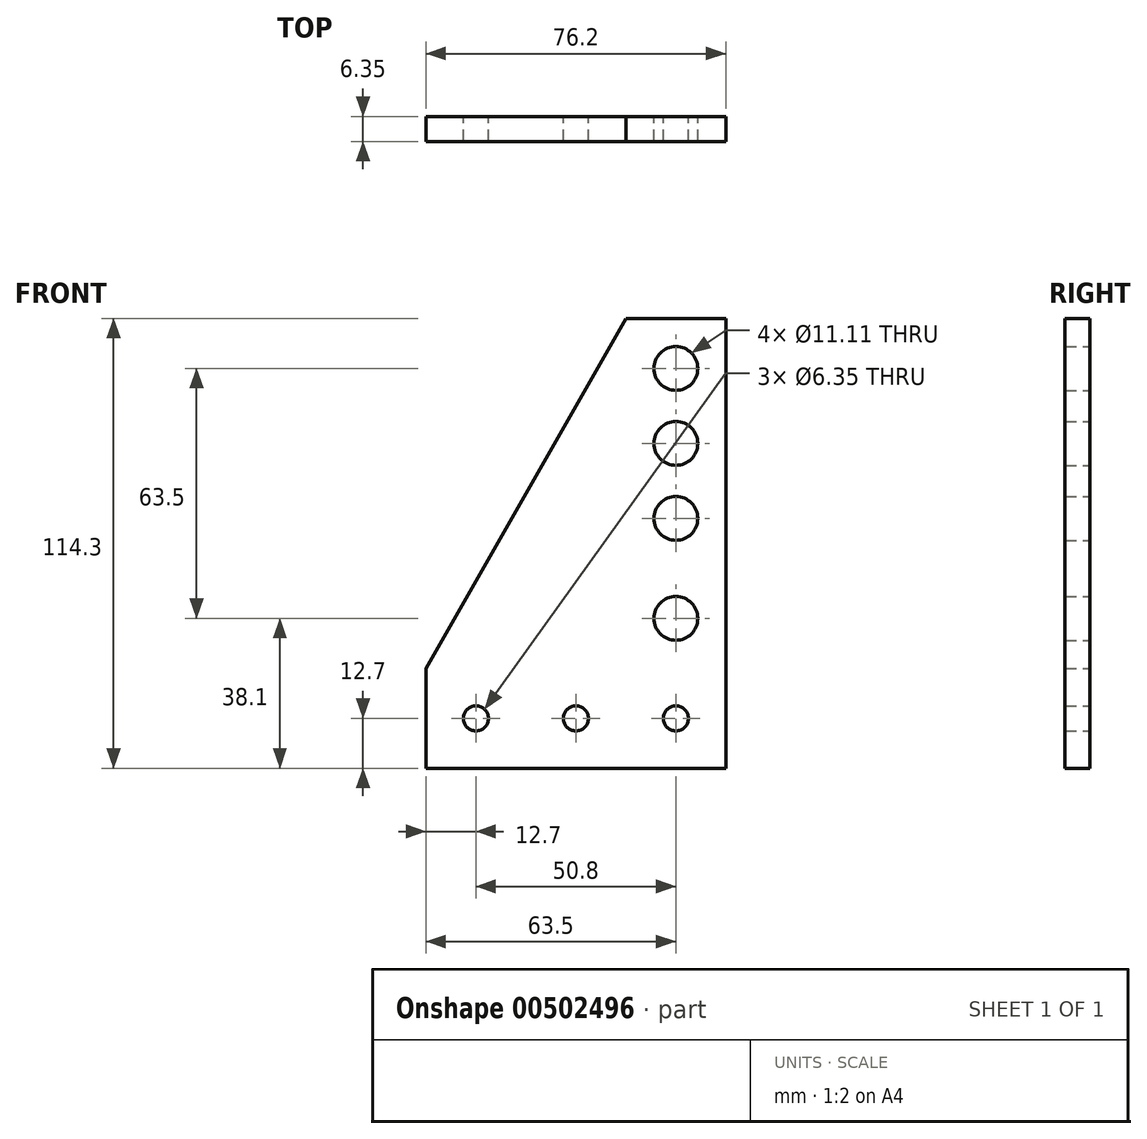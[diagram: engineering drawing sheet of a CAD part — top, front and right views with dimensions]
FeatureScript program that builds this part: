
annotation { "Feature Type Name" : "Feature", "Feature Type Description" : "" }
export const myFeature = defineFeature(function(context is Context, id is Id, definition is map)
    precondition{}
    {
        {
            var Q0;
            Q0=qCreatedBy(makeId("Front.planeOp"),FACE);
            var sketch = newSketch(context, id + "F0", { "sketchPlane" : qUnion([Q0])});
            skLineSegment(sketch, "E0.bottom", {"start": v(38.1, 57.15) * mm, "end": v(-38.1, 57.15) * mm});
            skLineSegment(sketch, "E0.top", {"start": v(38.1, -57.15) * mm, "end": v(-38.1, -57.15) * mm});
            skLineSegment(sketch, "E0.left", {"start": v(38.1, 57.15) * mm, "end": v(38.1, -57.15) * mm});
            skLineSegment(sketch, "E0.right", {"start": v(-38.1, 57.15) * mm, "end": v(-38.1, -57.15) * mm});
            skPoint(sketch, "E0.middle", {"position": v(0, 0) * mm});
            skLineSegment(sketch, "E1", {"start": v(-38.1, -44.45) * mm, "end": v(38.1, -44.45) * mm, "construction": true});
            skLineSegment(sketch, "E2", {"start": v(-38.1, -31.75) * mm, "end": v(38.1, -31.75) * mm, "construction": true});
            skCircle(sketch, "E3", {"center": v(-25.4, -44.45) * mm, "radius": 3.18 * mm});
            skCircle(sketch, "E4", {"center": v(0, -44.45) * mm, "radius": 3.18 * mm});
            skCircle(sketch, "E5", {"center": v(25.4, -44.45) * mm, "radius": 3.18 * mm});
            skLineSegment(sketch, "E6", {"start": v(25.4, -57.15) * mm, "end": v(25.4, 57.15) * mm, "construction": true});
            skCircle(sketch, "E7", {"center": v(25.4, -19.05) * mm, "radius": 5.56 * mm});
            skCircle(sketch, "E8", {"center": v(25.4, 44.45) * mm, "radius": 5.56 * mm});
            skCircle(sketch, "E9", {"center": v(25.4, 25.4) * mm, "radius": 5.56 * mm});
            skCircle(sketch, "E10", {"center": v(25.4, 6.35) * mm, "radius": 5.56 * mm});
            skLineSegment(sketch, "E11", {"start": v(12.7, 57.15) * mm, "end": v(12.7, -57.15) * mm, "construction": true});
            skLineSegment(sketch, "E12", {"start": v(12.7, 57.15) * mm, "end": v(-38.1, -31.75) * mm});
            skSolve(sketch);
        }
        {
            var Q0;
            {var subQ4=sQuery(id+"F0.wireOp",EDGE,"E0.top");Q0=makeQuery(id+"F0.imprint","IMPRINT",FACE,{"disambiguationData":[TD([[makeQuery(id+"F0.imprint","IMPRINT",EDGE,{"derivedFrom":subQ4}),-1.0]])]});}
            extrude(context, id + "F1", {"entities" : qUnion([Q0]), "depth" : 6.35 * mm, "offsetDistance" : 25.4 * mm});
        }
    });
